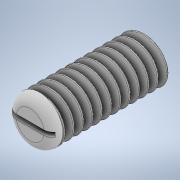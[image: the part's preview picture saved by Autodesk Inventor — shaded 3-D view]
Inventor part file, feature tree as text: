
AUTODESK INVENTOR PART (.ipt)
format: ipt  version: 2020 (Build 240168000, 168)  size: 713,728 bytes
history: native  units: in
note: dims shown in document units (in); Inventor stores cm internally (conversion verified against a paired STEP export)
features: sketch x5, extrude x2, revolve x2, fillet x1, thread x1, helix x1
ambient origin geometry x8: Origin, YZ Plane, XZ Plane, XY Plane, X Axis, Y Axis, Z Axis, Center Point
bodies: Solid1 (feature_tree), Solid2 (feature_tree)
feature tree (12):
  extrude  "Extrusion1"  Depth=0.625in TaperAngle=0.0deg
  fillet  "Fillet1"  Radius=0.05in
  thread  "Thread1"  [1 undecoded]
  revolve  "Revolution1"  [1 undecoded]
  revolve  "Revolution2"  [1 undecoded]
  helix  "Coil1"  [1 undecoded]
  extrude  "Extrusion2"  Depth=0.2291in
  sketch  "Sketch1"  dims[d0=0.25in d1=0.625in d2=0.0in d3=0.05in d4=0.575in d5=0.0in]
  sketch  "Sketch2"  dims[d6=0.3779in d7=0.008in d8=0.008in d11=0.05in]
  sketch  "Sketch3"  dims[d13=0.3779in d15=0.0in d16=0.0in]
  sketch  "Sketch4"  dims[d17=0.05in d18=0.675in d19=0.3937in d20=0.0in d21=0.0in d22=0.0in d23=0.0in d24=0.0in d25=0.2291in]
  sketch  "Sketch5"  dims[d26=0.025in d27=0.05in d28=0.0in]
note: 4 required parameter values undecoded (feature->parameter linkage not recoverable at this tier; creation-order binding heuristic only, values carry confidence <= 0.55)